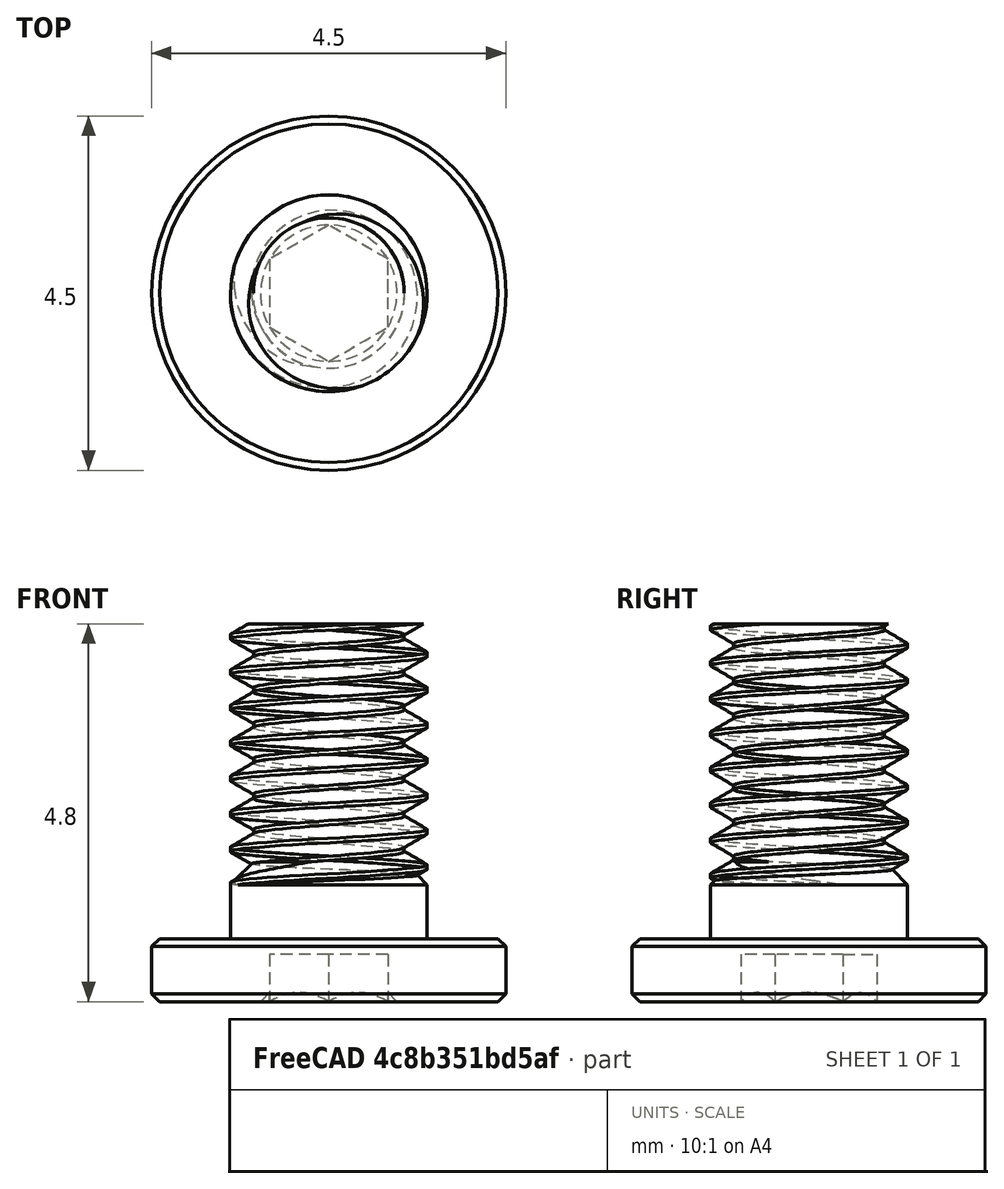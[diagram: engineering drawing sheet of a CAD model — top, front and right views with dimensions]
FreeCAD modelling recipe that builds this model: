
FCSTD DOCUMENT  (FreeCAD 0.20R29603 (Git))
Label: M2.5x4-ultra-low-profile-socket-head-bolt
License: Other
objects: Part::Feature×1, PartDesign::FeatureBase×1, PartDesign::Hole×1, PartDesign::Body×1
note: 5 computed .brp shape members not serialized (recipe doc carries the construction recipe); baked Part::Feature solids carry a one-line shape summary decoded from their .brp

FEATURE [Part::Feature] Part__Feature  label="90358A111_Ultra-Low-Profile Socket Head Screw"
  shape: bbox 4.501 x 4.501 x 6.983 mm, 77 faces (baked)
FEATURE [PartDesign::FeatureBase] BaseFeature
  BaseFeature = -> Part__Feature
FEATURE [PartDesign::Hole] Hole
  BaseFeature = -> BaseFeature
  CustomThreadClearance = 0
  Depth = 2
  DepthType = 0
  Diameter = 2.5
  DrillForDepth = false
  DrillPoint = 0
  DrillPointAngle = 118
  HoleCutCountersinkAngle = 90
  HoleCutCustomValues = false
  HoleCutDepth = 0
  HoleCutDiameter = 6.1
  HoleCutType = 0
  ModelThread = false
  Profile = -> BaseFeature [Face54]
  Tapered = false
  TaperedAngle = 90
  ThreadClass = 0
  ThreadDepth = 2
  ThreadDepthType = 0
  ThreadDirection = 0
  ThreadFit = 0
  ThreadSize = 9
  ThreadType = 1
  Threaded = true
  UseCustomThreadClearance = false
FEATURE [PartDesign::Body] Body
  BaseFeature = -> Part__Feature
  Group = -> [BaseFeature,Hole]
  Origin = -> Origin
  Tip = -> Hole
